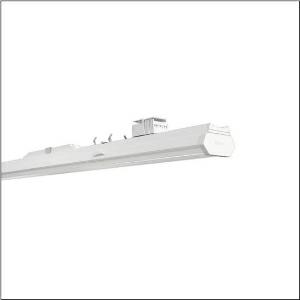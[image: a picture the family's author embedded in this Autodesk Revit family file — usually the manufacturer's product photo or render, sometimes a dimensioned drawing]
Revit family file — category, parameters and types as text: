
# Revit family: licross_11_protected_mo_51td1bdn49xg3c
name_source: partatom
category: Lighting Fixtures
units: mm (PartAtom-declared; Revit-internal decimal feet)

## family parameters
Cut with Voids When Loaded = No
Host = Face
Light Source = No
Part Type = Normal
Room Calculation Point = No
Round Connector Dimension = Use Diameter
Shared = No

## types (1)
- --- (1 x LED, 920 lm, 6.8 W, 4000K)
    Apparent Load = 7 VA
    CIE Flux Codes = 54 82 95 97 100
    Color Rendering = 80
    Color Temperature = 4000K
    Default Elevation = 1800 mm
    Description = Licross 11 Protected MO, luminaire insert, of sheet steel, galvanised, coil coated, white, length: 1.500mm, width: 90mm, height: 101mm, LED rated luminous flux: 9.370lm, light colour: 840, SDCM (Standard Deviation of Colour Matching)MacAdam ≤ 2 SDCM (initial), control gear: DALI 2 (for two DALI lines), with plug, 6-pole, with phase selection, for trunking rail, 14-core, mains connection: 220..240V, AC, 50/60Hz, rated input power: 61W, for trunking rail, 14-core, internal wiring halogen-free, for emergency light function, converter,control gear: single battery element, battery: LiFePO4, 9Ah, primary optical cover: cover, of PMMA, light emission: direct distribution, primary light characteristic: symmetric, protection rating (complete): IP54, insulation class (complete): insulation class I (protective earthing), certification: CE, UKCA, protection symbol: D if used in an environment with non-conductive dust loads with corresponding accessories, impact resistance: IK06, permissible ambient temperature for indoor applications: +5..+35°C, standard: EN 60598-2-22, LABS conformity tested according to VDMA 24364:2018-05, reducing of maximum allowable ambient temperature of 5°C with ceiling mounting, corresponds to IFS (International Featured Standards) requirements for safety and quality in the food industry, The light source and the operating device comply with the requirements of the Ecodesign Regulation (EU) 2019/2020 and are replaceable in accordance with this regulation, packaging unit: 1 piece
    Height = 92 mm
    Lamp = 1 x LED
    Lamp Light Flux = 920 lm
    Lamp Power = 6.8 W
    Lamp count = 1
    Length = 1500 mm
    Luminous efficacy = 135 lm/W
    Manufacturer = Siteco
    ModVariant = No
    Model = 51TD1BDN49XG3C
    Mounting Place = Ceiling
    Mounting Type = Pendant
    Number of Poles = 1
    OnlyDefault = Yes
    Power Factor = 1
    Product Name = Licross 11 Protected MO
    Product group = luminaire insert | ceiling pendant
    ProductGroupID = 901
    Protection Class = Protection class I
    Protection Degree = IP 54
    RLX_Detail_Level = 1
    RLX_Emergency_Light_Flux = 0 lm
    RLX_Emergency_Type = 0
    RLX_Emergency_Type_DB = No
    RlxData = <blob elided: 24921 chars, md5=8dfa0c8b>
    Socket = socket
    Standby Power = 0 W
    System Light Flux = 920 lm
    System Power = 7 W
    Type Comments = : emergency light operation: 3 h
    Type Image = l_1256145.jpg
    URL = http://relux.com
    VarID = @adj_095007
    Voltage = 0 V
    Weight = 0.00 kg
    Width = 88 mm

## geometry (parser evidence)
native form markers: Blend x4, Sweep x10
no freeform markers — native parametric forms only
